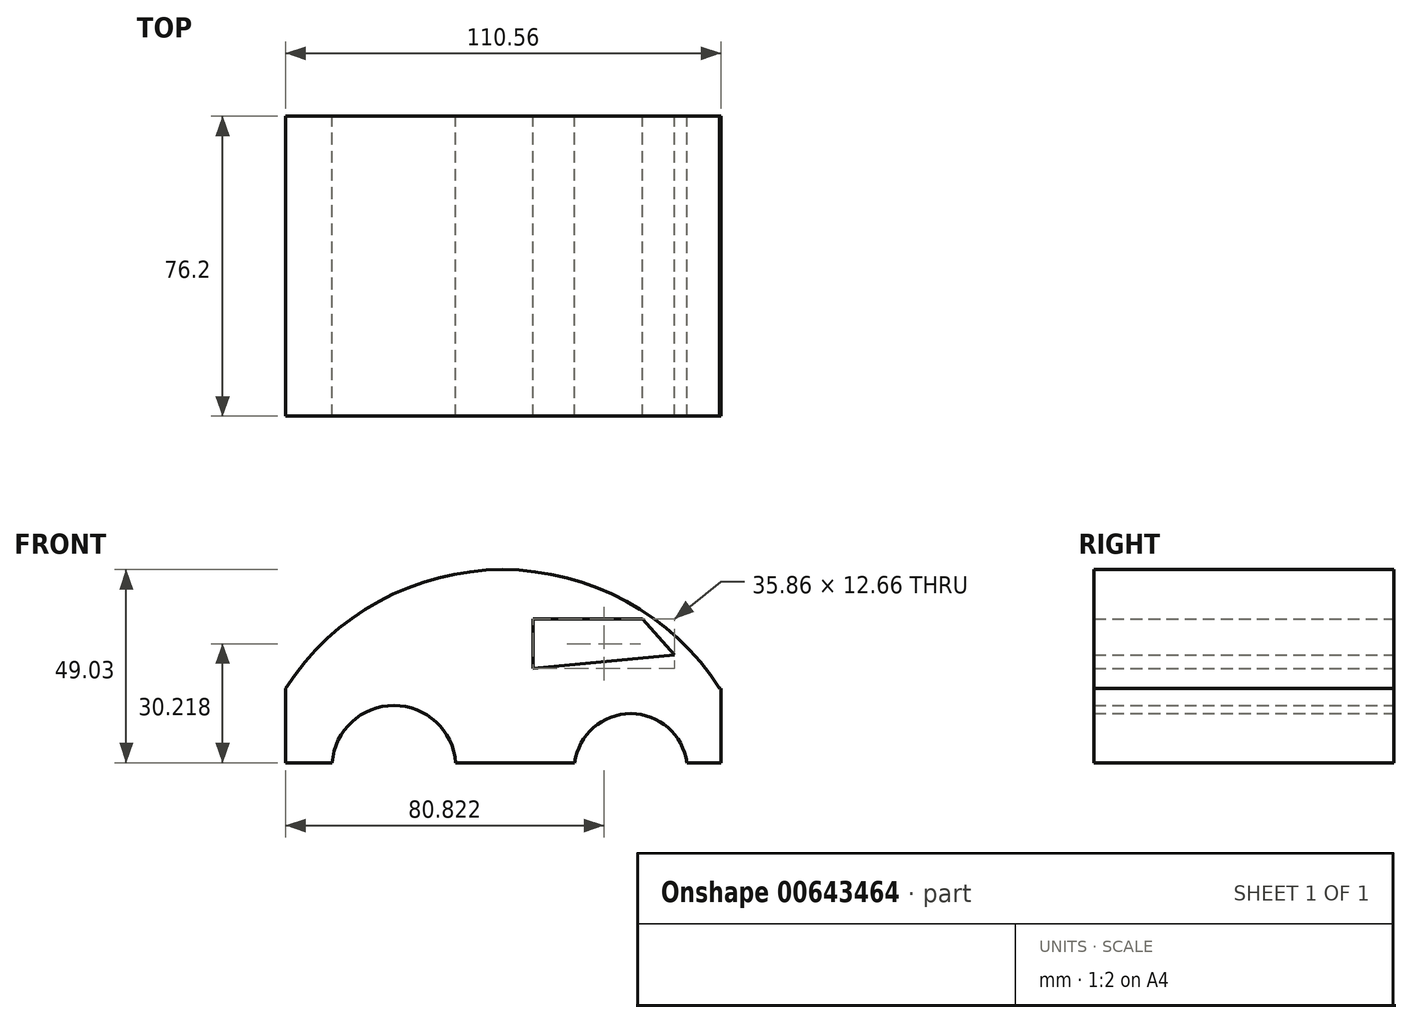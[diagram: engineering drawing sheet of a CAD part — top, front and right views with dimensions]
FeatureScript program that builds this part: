
annotation { "Feature Type Name" : "Feature", "Feature Type Description" : "" }
export const myFeature = defineFeature(function(context is Context, id is Id, definition is map)
    precondition{}
    {
        {
            var Q0;
            Q0=qCreatedBy(makeId("Front.planeOp"),FACE);
            var sketch = newSketch(context, id + "F0", { "sketchPlane" : qUnion([Q0])});
            skArc(sketch, "E0", {"start": v(47.34, 0) * mm, "mid": v(-7.77, 30.18) * mm, "end": v(-62.89, 0) * mm});
            skLineSegment(sketch, "E1.left", {"start": v(-62.89, 0) * mm, "end": v(-62.89, 0) * mm});
            skLineSegment(sketch, "E1.right", {"start": v(47.34, 0) * mm, "end": v(47.34, 0) * mm});
            skLineSegment(sketch, "E2.bottom", {"start": v(47.34, 0) * mm, "end": v(47.67, 0) * mm});
            skLineSegment(sketch, "E2.top", {"start": v(-62.89, -18.85) * mm, "end": v(-51.08, -18.85) * mm});
            skLineSegment(sketch, "E2.left", {"start": v(-62.89, 0) * mm, "end": v(-62.89, -18.85) * mm});
            skLineSegment(sketch, "E2.right", {"start": v(47.67, 0) * mm, "end": v(47.67, -18.85) * mm});
            skArc(sketch, "E3", {"start": v(-19.7, -18.85) * mm, "mid": v(-35.4, -4.33) * mm, "end": v(-51.08, -18.85) * mm});
            skArc(sketch, "E4", {"start": v(39.03, -18.85) * mm, "mid": v(24.78, -6.4) * mm, "end": v(10.53, -18.85) * mm});
            skLineSegment(sketch, "E5.trimOffspring", {"start": v(-19.7, -18.85) * mm, "end": v(10.53, -18.85) * mm});
            skLineSegment(sketch, "E6.trimOffspring", {"start": v(39.03, -18.85) * mm, "end": v(47.67, -18.85) * mm});
            skLineSegment(sketch, "E7", {"start": v(18.01, 17.7) * mm, "end": v(0, 17.7) * mm});
            skLineSegment(sketch, "E8", {"start": v(0, 17.7) * mm, "end": v(0, 5.04) * mm});
            skLineSegment(sketch, "E9", {"start": v(18.01, 17.7) * mm, "end": v(27.8, 17.7) * mm});
            skLineSegment(sketch, "E10", {"start": v(27.8, 17.7) * mm, "end": v(35.86, 8.5) * mm});
            skLineSegment(sketch, "E11", {"start": v(35.86, 8.5) * mm, "end": v(0, 5.04) * mm});
            skLineSegment(sketch, "E12", {"start": v(-43.89, 11.94) * mm, "end": v(-43.89, 5.04) * mm});
            skLineSegment(sketch, "E13", {"start": v(-43.89, 11.94) * mm, "end": v(-18.55, 11.94) * mm});
            skLineSegment(sketch, "E14", {"start": v(-41.87, 5.04) * mm, "end": v(-18.84, 5.04) * mm});
            skLineSegment(sketch, "E15", {"start": v(-18.55, 11.94) * mm, "end": v(-18.84, 5.04) * mm});
            skSolve(sketch);
        }
        {
            var Q0;
            Q0 = qSketchRegion(id + "F0", true);
            extrude(context, id + "F1", {"entities" : qUnion([Q0]), "depth" : 76.2 * mm, "offsetDistance" : 25.4 * mm});
        }
    });
